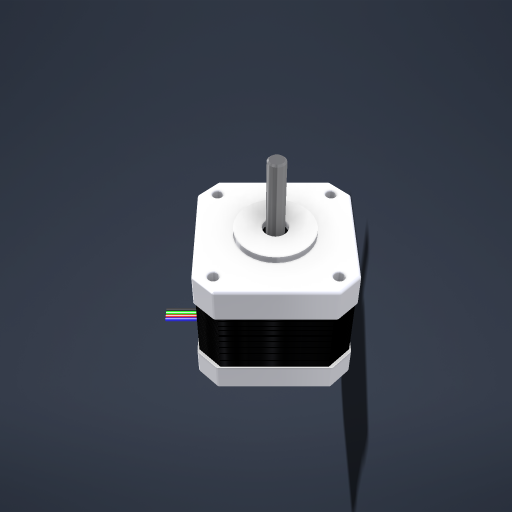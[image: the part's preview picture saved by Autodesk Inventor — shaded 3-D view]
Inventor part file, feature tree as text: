
AUTODESK INVENTOR PART (.ipt)
format: ipt  version: 2023 (Build 270158000, 158)  size: 977,920 bytes
history: native  units: mm
features: extrude x12, sketch x4, hole x4, fillet x4, chamfer x2, plane x1, pattern_linear x1, projected_geometry x1
ambient origin geometry x8: Origin, YZ Plane, XZ Plane, XY Plane, X Axis, Y Axis, Z Axis, Center Point
bodies: Solid1 (feature_tree)
feature tree (29):
  sketch  "Sketch1"  dims[d0=7.0mm d1=22.0mm]
  extrude  "Extrusion1"  Depth=22.0mm
  extrude  "Extrusion2"  Depth=31.0mm
  extrude  "Extrusion3"  Depth=3.0mm
  plane  "Work Plane2"
  extrude  "Extrusion7"  Depth=10.0mm
  extrude  "Extrusion8"  Depth=10.0mm
  chamfer  "Chamfer1"  Distance=42.0mm
  pattern_linear  "Rectangular Pattern2"  Spacing1=42.0mm  [1 undecoded]
  hole  "Hole1"  [1 undecoded]
  hole  "Hole2"  [1 undecoded]
  hole  "Hole3"  [1 undecoded]
  hole  "Hole4"  [1 undecoded]
  extrude  "Extrusion9"  Depth=10.0mm
  fillet  "Fillet1"  Radius=24.0mm
  fillet  "Fillet2"  Radius=2.0mm
  chamfer  "Chamfer2"  Distance=39.0mm
  fillet  "Fillet3"  [1 undecoded]
  sketch  "Sketch6"  dims[d10=3.0mm d11=3.0mm d12=3.0mm d39=42.0mm d40=42.0mm d41=135.0deg d42=51.618795mm d43=51.618795mm d44=25.809398mm d45=25.809398mm d46=24.0mm d47=0.0mm d48=2.0mm d49=0.0mm d50=39.0mm d51=0.0mm d60=-10.0mm d126=20.0mm d127=0.0mm d128=1.0mm d129=1.0mm d130=1.0mm d131=1.0mm d132=0.5mm d134=0.5mm d135=0.5mm d136=0.5mm d137=0.5mm d138=1.0mm d139=1.0mm d140=0.5mm d141=0.0mm d145=0.125mm d146=2.0mm d147=45.0deg d148=560.0mm d150=0.5mm d151=10.0mm d152=10.0mm d153=6.0mm d154=6.0mm d155=4.0mm d156=2.0mm d157=90.0deg d158=3.0mm d159=0.0mm d160=10.0mm d161=10.0mm d162=6.0mm d163=6.0mm d164=4.0mm d165=2.0mm d166=90.0deg d167=3.0mm d168=0.0mm d169=10.0mm d170=10.0mm d171=6.0mm d172=6.0mm d173=4.0mm d174=2.0mm d175=90.0deg d176=3.0mm d177=0.0mm d178=10.0mm d179=10.0mm d180=6.0mm d181=6.0mm d182=4.0mm d183=2.0mm d184=90.0deg d185=3.0mm d186=0.0mm d187=41.0mm d188=0.0mm d189=40.0mm d190=0.0mm d191=1.0mm d192=1.0mm d193=0.5mm d194=2.0mm d195=45.0deg d196=0.5mm d197=1.2mm d198=40.0mm d200=1.2mm d201=10.0mm d203=10.0mm d205=2.5mm d206=2.5mm d207=1.0mm d208=0.0mm d209=0.3mm d210=10.0mm d211=0.0mm d212=10.0mm d213=0.0mm d214=10.0mm d215=0.0mm d216=10.0mm d217=0.0mm d218=0.2mm d219=5.0mm d220=0.0mm d221=0.0mm d225=0.5mm d226=0.872665mm d227=0.5mm d228=0.872665mm]
  extrude  "Extrusion10"  Depth=10.0mm TaperAngle=0.0deg
  fillet  "Fillet4"  Radius=1.0mm
  extrude  "Extrusion11"  Depth=10.0mm
  extrude  "Extrusion12"  Depth=10.0mm
  extrude  "Extrusion13"  Depth=10.0mm
  extrude  "Extrusion14"  Depth=10.0mm
  extrude  "Extrusion15"  Depth=10.0mm
  sketch  "Sketch4"  dims[d4=5.0mm d5=31.0mm]
  projected_geometry  "Projected Loop2"
  sketch  "Sketch5"  dims[d6=31.0mm d9=3.0mm]
note: 6 required parameter values undecoded (feature->parameter linkage not recoverable at this tier; creation-order binding heuristic only, values carry confidence <= 0.55)
